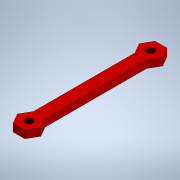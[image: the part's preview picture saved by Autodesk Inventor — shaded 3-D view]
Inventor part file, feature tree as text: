
AUTODESK INVENTOR PART (.ipt)
format: ipt  version: 2020 (Build 240168000, 168)  size: 125,440 bytes
history: native  units: in
note: dims shown in document units (in); Inventor stores cm internally (conversion verified against a paired STEP export)
features: extrude x1, sketch x1
ambient origin geometry x8: Origin, YZ Plane, XZ Plane, XY Plane, X Axis, Y Axis, Z Axis, Center Point
bodies: Solid1 (feature_tree)
feature tree (2):
  extrude  "Extrusion1"  Depth=0.315in
  sketch  "Sketch1"  dims[d1=1.5748in d2=0.315in d3=0.122in d4=0.122in d5=0.1181in d6=0.0in]
